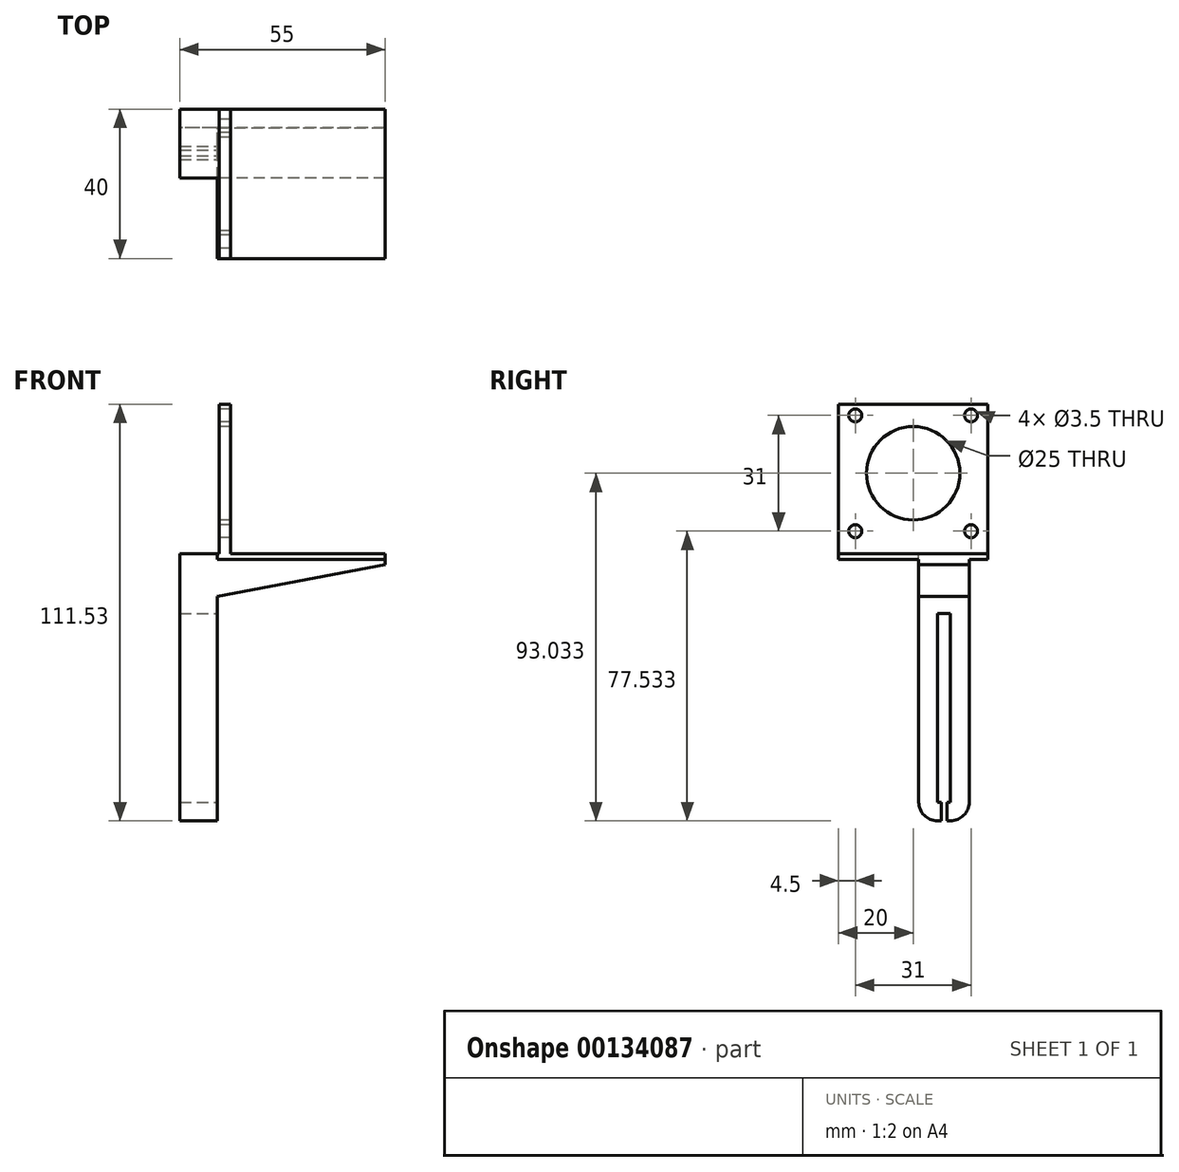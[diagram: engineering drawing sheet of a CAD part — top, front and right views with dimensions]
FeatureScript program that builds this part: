
annotation { "Feature Type Name" : "Feature", "Feature Type Description" : "" }
export const myFeature = defineFeature(function(context is Context, id is Id, definition is map)
    precondition{}
    {
        {
            var Q0;
            Q0=qCreatedBy(makeId("Right.planeOp"),FACE);
            var sketch = newSketch(context, id + "F0", { "sketchPlane" : qUnion([Q0])});
            skLineSegment(sketch, "E0.bottom", {"start": v(-5, 0) * mm, "end": v(-8.5, 0) * mm});
            skLineSegment(sketch, "E0.top", {"start": v(0, 70) * mm, "end": v(-13.5, 70) * mm});
            skLineSegment(sketch, "E0.left", {"start": v(0, 5) * mm, "end": v(0, 70) * mm});
            skLineSegment(sketch, "E0.right", {"start": v(-13.5, 5) * mm, "end": v(-13.5, 70) * mm});
            skPoint(sketch, "E1.visualSharp", {"position": v(-13.5, 0) * mm});
            skArc(sketch, "E1.filletArc", {"start": v(-13.5, 5) * mm, "mid": v(-12.04, 1.46) * mm, "end": v(-8.5, 0) * mm});
            skPoint(sketch, "E2.visualSharp", {"position": v(0, 0) * mm});
            skArc(sketch, "E2.filletArc", {"start": v(-5, 0) * mm, "mid": v(-1.46, 1.46) * mm, "end": v(0, 5) * mm});
            skSolve(sketch);
        }
        {
            var Q0;
            Q0 = qSketchRegion(id + "F0", true);
            extrude(context, id + "F1", {"entities" : qUnion([Q0]), "depth" : 10 * mm});
        }
        {
            var Q0;
            Q0=makeQuery(id+"F1.opExtrude","CAP_FACE",FACE,{"disambiguationData":[OSD([sQuery(id+"F0.wireOp",EDGE,"E0.bottom"),sQuery(id+"F0.wireOp",EDGE,"E0.top"),sQuery(id+"F0.wireOp",EDGE,"E0.left"),sQuery(id+"F0.wireOp",EDGE,"E0.right"),sQuery(id+"F0.wireOp",EDGE,"E1.filletArc"),sQuery(id+"F0.wireOp",EDGE,"E2.filletArc")])],"isStart":false});
            var sketch = newSketch(context, id + "F2", { "sketchPlane" : qUnion([Q0])});
            skLineSegment(sketch, "E3.bottom", {"start": v(-8.5, 55.5) * mm, "end": v(-5, 55.5) * mm});
            skLineSegment(sketch, "E3.top", {"start": v(-8.5, 5) * mm, "end": v(-5, 5) * mm});
            skLineSegment(sketch, "E3.left", {"start": v(-8.5, 55.5) * mm, "end": v(-8.5, 5) * mm});
            skLineSegment(sketch, "E3.right", {"start": v(-5, 55.5) * mm, "end": v(-5, 5) * mm});
            skLineSegment(sketch, "E4", {"start": v(-13.5, 37.5) * mm, "end": v(-8.5, 37.5) * mm, "construction": true});
            skLineSegment(sketch, "E5", {"start": v(-5, 37.5) * mm, "end": v(0, 37.5) * mm, "construction": true});
            skPoint(sketch, "E5.startSnap0", {"position": v(-5, 30.25) * mm});
            skLineSegment(sketch, "E6.bottom", {"start": v(-7.44, 0) * mm, "end": v(-5.94, 0) * mm});
            skLineSegment(sketch, "E6.top", {"start": v(-7.44, 5) * mm, "end": v(-5.94, 5) * mm});
            skLineSegment(sketch, "E6.left", {"start": v(-7.44, 0) * mm, "end": v(-7.44, 5) * mm});
            skLineSegment(sketch, "E6.right", {"start": v(-5.94, 0) * mm, "end": v(-5.94, 5) * mm});
            skSolve(sketch);
        }
        {
            var Q0;
            Q0 = qSketchRegion(id + "F2", true);
            extrude(context, id + "F3", {"entities" : qUnion([Q0]), "operationType" : NewBodyOperationType.REMOVE, "oppositeDirection" : true, "depth" : 11 * mm});
        }
        {
            var Q0;
            Q0=qCreatedBy(makeId("Front.planeOp"),FACE);
            var sketch = newSketch(context, id + "F4", { "sketchPlane" : qUnion([Q0])});
            skLineSegment(sketch, "E7.bottom", {"start": v(0, 71.53) * mm, "end": v(55, 71.53) * mm});
            skLineSegment(sketch, "E7.top", {"start": v(0, 70) * mm, "end": v(55, 70) * mm});
            skLineSegment(sketch, "E7.left", {"start": v(0, 71.53) * mm, "end": v(0, 70) * mm});
            skLineSegment(sketch, "E7.right", {"start": v(55, 71.53) * mm, "end": v(55, 70) * mm});
            skLineSegment(sketch, "E8.bottom", {"start": v(10.55, 71.53) * mm, "end": v(13.55, 71.53) * mm});
            skLineSegment(sketch, "E8.top", {"start": v(10.55, 111.53) * mm, "end": v(13.55, 111.53) * mm});
            skLineSegment(sketch, "E8.left", {"start": v(10.55, 71.53) * mm, "end": v(10.55, 111.53) * mm});
            skLineSegment(sketch, "E8.right", {"start": v(13.55, 71.53) * mm, "end": v(13.55, 111.53) * mm});
            skSolve(sketch);
        }
        {
            var Q0;
            Q0 = qSketchRegion(id + "F4", true);
            extrude(context, id + "F5", {"entities" : qUnion([Q0]), "operationType" : NewBodyOperationType.ADD, "depth" : 35 * mm, "hasSecondDirection" : true, "secondDirectionOppositeDirection" : true, "secondDirectionDepth" : 5 * mm});
        }
        {
            var Q0;
            Q0=makeQuery(id+"F1.opExtrude","CAP_FACE",FACE,{"disambiguationData":[OSD([sQuery(id+"F0.wireOp",EDGE,"E0.bottom"),sQuery(id+"F0.wireOp",EDGE,"E0.top"),sQuery(id+"F0.wireOp",EDGE,"E0.left"),sQuery(id+"F0.wireOp",EDGE,"E0.right"),sQuery(id+"F0.wireOp",EDGE,"E1.filletArc"),sQuery(id+"F0.wireOp",EDGE,"E2.filletArc")])],"isStart":false});
            var sketch = newSketch(context, id + "F6", { "sketchPlane" : qUnion([Q0])});
            skLineSegment(sketch, "E9.bottom", {"start": v(-13.5, 70) * mm, "end": v(0, 70) * mm});
            skLineSegment(sketch, "E9.top", {"start": v(-13.5, 60) * mm, "end": v(0, 60) * mm});
            skLineSegment(sketch, "E9.left", {"start": v(-13.5, 70) * mm, "end": v(-13.5, 60) * mm});
            skLineSegment(sketch, "E9.right", {"start": v(0, 70) * mm, "end": v(0, 60) * mm});
            skSolve(sketch);
        }
        {
            var Q0;
            Q0 = qSketchRegion(id + "F6", true);
            var Q1;
            Q1=makeQuery(id+"F5.opExtrude","SWEPT_FACE",FACE,{"disambiguationData":[OSD([sQuery(id+"F4.wireOp",EDGE,"E7.right")])]});
            extrude(context, id + "F7", {"entities" : qUnion([Q0]), "operationType" : NewBodyOperationType.ADD, "endBound" : BoundingType.UP_TO_SURFACE, "endBoundEntityFace" : qUnion([Q1]), "depth" : 45 * mm});
        }
        {
            var Q0;
            Q0=makeQuery(id+"F7.boolean.opBoolean","MERGE",FACE,{"derivedFrom":[makeQuery(id+"F1.opExtrude","SWEPT_FACE",FACE,{"disambiguationData":[OSD([sQuery(id+"F0.wireOp",EDGE,"E0.right")])]}),makeQuery(id+"F7.opExtrude","SWEPT_FACE",FACE,{"disambiguationData":[OSD([sQuery(id+"F6.wireOp",EDGE,"E9.left")])]})]});
            var sketch = newSketch(context, id + "F8", { "sketchPlane" : qUnion([Q0])});
            skLineSegment(sketch, "E10", {"start": v(10, 60) * mm, "end": v(55, 68.61) * mm});
            skLineSegment(sketch, "E11", {"start": v(55, 68.61) * mm, "end": v(55, 60) * mm});
            skLineSegment(sketch, "E12", {"start": v(55, 60) * mm, "end": v(10, 60) * mm});
            skSolve(sketch);
        }
        {
            var Q0;
            Q0 = qSketchRegion(id + "F8", true);
            extrude(context, id + "F9", {"entities" : qUnion([Q0]), "operationType" : NewBodyOperationType.REMOVE, "oppositeDirection" : true, "depth" : 15 * mm});
        }
        {
            var Q0;
            Q0=makeQuery(id+"F5.opExtrude","SWEPT_FACE",FACE,{"disambiguationData":[OSD([sQuery(id+"F4.wireOp",EDGE,"E8.left")])]});
            var sketch = newSketch(context, id + "F10", { "sketchPlane" : qUnion([Q0])});
            skLineSegment(sketch, "E13.bottom", {"start": v(-0.5, 108.53) * mm, "end": v(30.5, 108.53) * mm, "construction": true});
            skLineSegment(sketch, "E13.top", {"start": v(-0.5, 77.53) * mm, "end": v(30.5, 77.53) * mm, "construction": true});
            skLineSegment(sketch, "E13.left", {"start": v(-0.5, 108.53) * mm, "end": v(-0.5, 77.53) * mm, "construction": true});
            skLineSegment(sketch, "E13.right", {"start": v(30.5, 108.53) * mm, "end": v(30.5, 77.53) * mm, "construction": true});
            skCircle(sketch, "E14", {"center": v(-0.5, 108.53) * mm, "radius": 1.75 * mm});
            skCircle(sketch, "E15", {"center": v(30.5, 108.53) * mm, "radius": 1.75 * mm});
            skCircle(sketch, "E16", {"center": v(30.5, 77.53) * mm, "radius": 1.75 * mm});
            skCircle(sketch, "E17", {"center": v(-0.5, 77.53) * mm, "radius": 1.75 * mm});
            skLineSegment(sketch, "E18", {"start": v(15, 77.53) * mm, "end": v(15, 71.53) * mm, "construction": true});
            skLineSegment(sketch, "E19", {"start": v(-5, 93.05) * mm, "end": v(-0.5, 93.05) * mm, "construction": true});
            skLineSegment(sketch, "E20", {"start": v(30.5, 93.05) * mm, "end": v(35, 93.05) * mm, "construction": true});
            skLineSegment(sketch, "E21", {"start": v(-0.5, 108.53) * mm, "end": v(30.5, 77.53) * mm, "construction": true});
            skLineSegment(sketch, "E22", {"start": v(30.5, 108.53) * mm, "end": v(-0.5, 77.53) * mm, "construction": true});
            skCircle(sketch, "E23", {"center": v(15, 93.03) * mm, "radius": 12.5 * mm});
            skSolve(sketch);
        }
        {
            var Q0;
            Q0 = qSketchRegion(id + "F10", true);
            extrude(context, id + "F11", {"entities" : qUnion([Q0]), "operationType" : NewBodyOperationType.REMOVE, "oppositeDirection" : true, "depth" : 25 * mm});
        }
        {
            var Q0;
            {var subQ0=sQuery(id+"F4.wireOp",EDGE,"E7.bottom");Q0=makeQuery(id+"F5.opExtrude","SWEPT_FACE",FACE,{"disambiguationData":[OSD([subQ0]),TDD([makeQuery(id+"F4.imprint","IMPRINT",EDGE,{"disambiguationData":[TD([[makeQuery(id+"F4.imprint","INTERSECT",VERTEX,{"derivedFrom":[subQ0,sQuery(id+"F4.wireOp",EDGE,"E7.right")]}),1.0]])],"derivedFrom":subQ0})])]});}
            var sketch = newSketch(context, id + "F12", { "sketchPlane" : qUnion([Q0])});
            skLineSegment(sketch, "E24.bottom", {"start": v(10, -13.5) * mm, "end": v(0, -13.5) * mm});
            skLineSegment(sketch, "E24.top", {"start": v(10, -35) * mm, "end": v(0, -35) * mm});
            skLineSegment(sketch, "E24.left", {"start": v(10, -13.5) * mm, "end": v(10, -35) * mm});
            skLineSegment(sketch, "E24.right", {"start": v(0, -13.5) * mm, "end": v(0, -35) * mm});
            skSolve(sketch);
        }
        {
            var Q0;
            Q0 = qSketchRegion(id + "F12", true);
            extrude(context, id + "F13", {"entities" : qUnion([Q0]), "operationType" : NewBodyOperationType.REMOVE, "oppositeDirection" : true, "depth" : 25 * mm});
        }
    });
